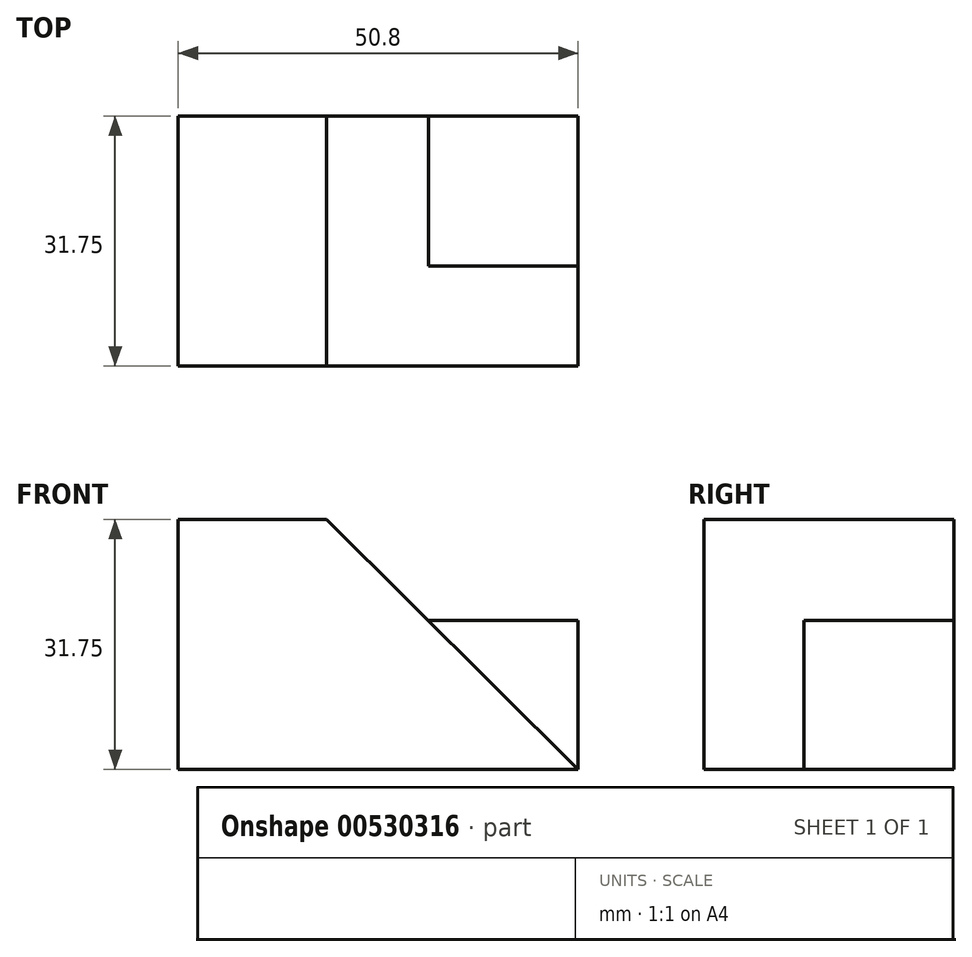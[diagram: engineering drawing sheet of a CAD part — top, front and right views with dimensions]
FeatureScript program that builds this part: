
annotation { "Feature Type Name" : "Feature", "Feature Type Description" : "" }
export const myFeature = defineFeature(function(context is Context, id is Id, definition is map)
    precondition{}
    {
        {
            var Q0;
            Q0=qCreatedBy(makeId("Front.planeOp"),FACE);
            var sketch = newSketch(context, id + "F0", { "sketchPlane" : qUnion([Q0])});
            skLineSegment(sketch, "E0", {"start": v(-66.1, 45.01) * mm, "end": v(-66.1, 13.26) * mm});
            skLineSegment(sketch, "E1", {"start": v(-66.1, 13.26) * mm, "end": v(-15.3, 13.26) * mm});
            skLineSegment(sketch, "E2", {"start": v(-15.3, 13.26) * mm, "end": v(-15.3, 45.01) * mm});
            skLineSegment(sketch, "E3", {"start": v(-15.3, 45.01) * mm, "end": v(-66.1, 45.01) * mm});
            skSolve(sketch);
        }
        {
            var Q0;
            Q0=makeQuery(id+"F0.imprint","IMPRINT",FACE,{"disambiguationData":[TD([[makeQuery(id+"F0.imprint","IMPRINT",EDGE,{"derivedFrom":sQuery(id+"F0.wireOp",EDGE,"E0")}),1.0]])]});
            extrude(context, id + "F1", {"entities" : qUnion([Q0]), "depth" : 31.75 * mm, "offsetDistance" : 25.4 * mm});
        }
        {
            var Q0;
            Q0=makeQuery(id+"F1.opExtrude","CAP_FACE",FACE,{"disambiguationData":[OSD([sQuery(id+"F0.wireOp",EDGE,"E0"),sQuery(id+"F0.wireOp",EDGE,"E1"),sQuery(id+"F0.wireOp",EDGE,"E2"),sQuery(id+"F0.wireOp",EDGE,"E3")])],"isStart":false});
            var sketch = newSketch(context, id + "F2", { "sketchPlane" : qUnion([Q0])});
            skLineSegment(sketch, "E4", {"start": v(-15.3, 45.01) * mm, "end": v(-47.24, 45.01) * mm});
            skLineSegment(sketch, "E5", {"start": v(-47.24, 45.01) * mm, "end": v(-15.3, 13.26) * mm});
            skSolve(sketch);
        }
        {
            var Q0;
            Q0=makeQuery(id+"F2.imprint","IMPRINT",FACE,{"disambiguationData":[TD([[makeQuery(id+"F2.imprint","IMPRINT",EDGE,{"derivedFrom":sQuery(id+"F2.wireOp",EDGE,"E4")}),1.0]])]});
            extrude(context, id + "F3", {"entities" : qUnion([Q0]), "operationType" : NewBodyOperationType.REMOVE, "oppositeDirection" : true, "depth" : 12.7 * mm, "offsetDistance" : 25.4 * mm});
        }
        {
            var Q0;
            Q0=makeQuery(id+"F3.boolean.opBoolean","COPY",FACE,{"derivedFrom":makeQuery(id+"F3.opExtrude","CAP_FACE",FACE,{"disambiguationData":[OSD([sQuery(id+"F0.wireOp",EDGE,"E2"),sQuery(id+"F2.wireOp",EDGE,"E4"),sQuery(id+"F2.wireOp",EDGE,"E5")])],"isStart":false})});
            var sketch = newSketch(context, id + "F4", { "sketchPlane" : qUnion([Q0])});
            skLineSegment(sketch, "E6", {"start": v(-15.3, 13.26) * mm, "end": v(-15.3, 32.16) * mm});
            skLineSegment(sketch, "E7", {"start": v(-15.3, 32.16) * mm, "end": v(-34.32, 32.16) * mm});
            skSolve(sketch);
        }
        {
            var Q0;
            {var subQ0=sQuery(id+"F4.wireOp",EDGE,"E7");Q0=makeQuery(id+"F4.imprint","IMPRINT",FACE,{"disambiguationData":[TD([[makeQuery(id+"F4.imprint","IMPRINT",EDGE,{"derivedFrom":subQ0}),-1.0]])]});}
            extrude(context, id + "F5", {"entities" : qUnion([Q0]), "operationType" : NewBodyOperationType.REMOVE, "endBound" : BoundingType.THROUGH_ALL, "oppositeDirection" : true, "depth" : 25.4 * mm, "offsetDistance" : 25.4 * mm});
        }
    });
